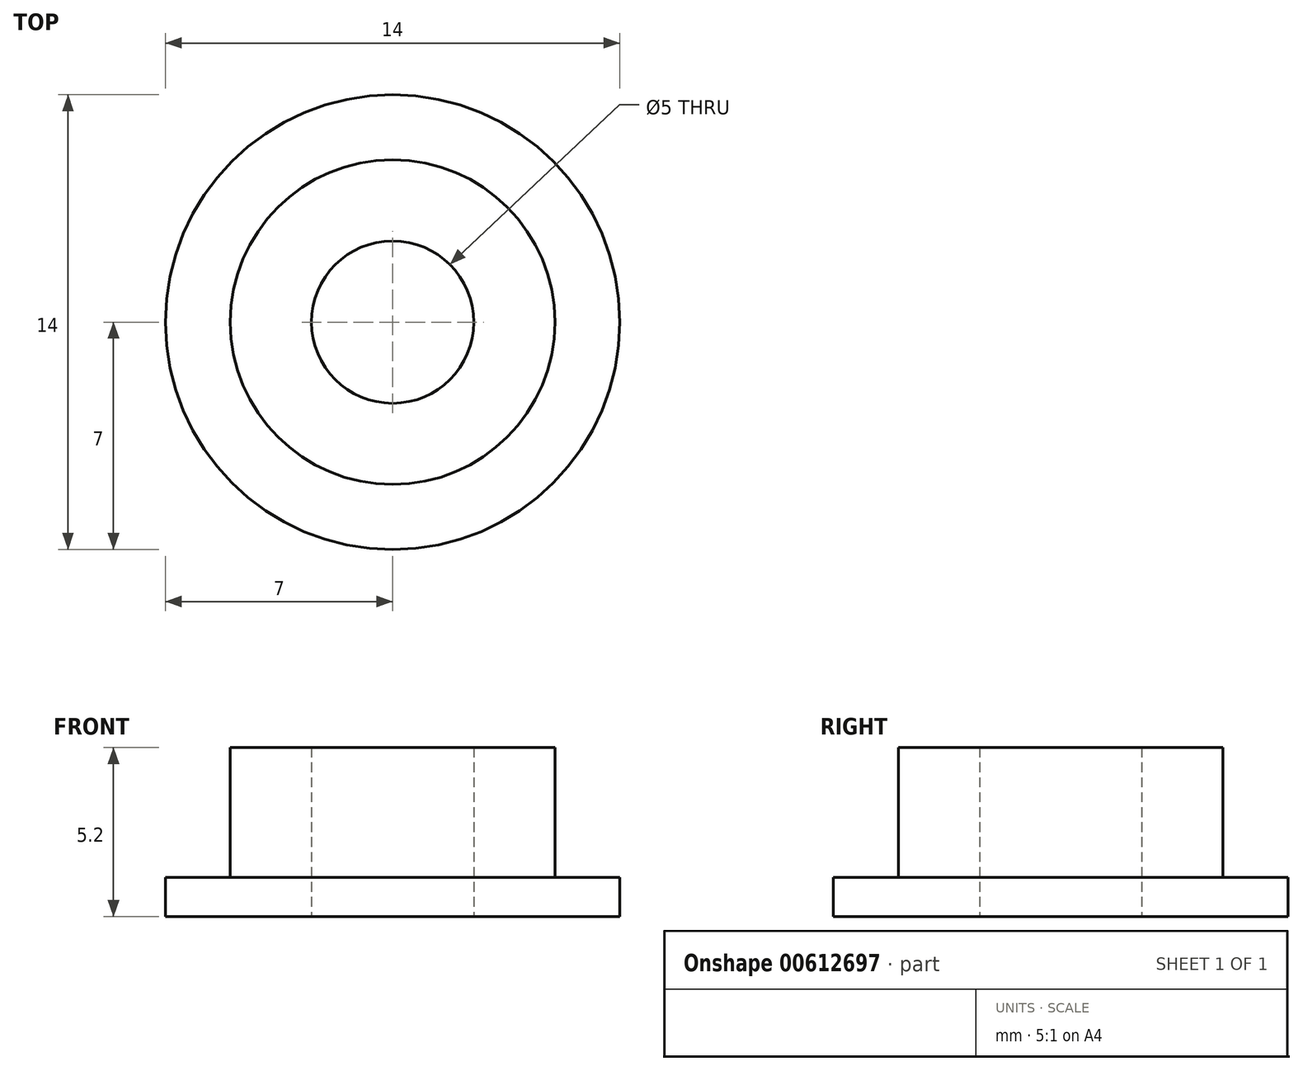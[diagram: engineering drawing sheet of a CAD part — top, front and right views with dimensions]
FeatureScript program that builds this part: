
annotation { "Feature Type Name" : "Feature", "Feature Type Description" : "" }
export const myFeature = defineFeature(function(context is Context, id is Id, definition is map)
    precondition{}
    {
        {
            var Q0;
            Q0=qCreatedBy(makeId("Front.planeOp"),FACE);
            var sketch = newSketch(context, id + "F0", { "sketchPlane" : qUnion([Q0])});
            skLineSegment(sketch, "E0", {"start": v(2.5, 0) * mm, "end": v(2.5, 5.2) * mm});
            skLineSegment(sketch, "E1", {"start": v(2.5, 5.2) * mm, "end": v(5, 5.2) * mm});
            skLineSegment(sketch, "E2", {"start": v(5, 5.2) * mm, "end": v(5, 1.2) * mm});
            skLineSegment(sketch, "E3", {"start": v(5, 1.2) * mm, "end": v(7, 1.2) * mm});
            skLineSegment(sketch, "E4", {"start": v(7, 1.2) * mm, "end": v(7, 0) * mm});
            skLineSegment(sketch, "E5", {"start": v(7, 0) * mm, "end": v(2.5, 0) * mm});
            skLineSegment(sketch, "E6", {"start": v(0, 0) * mm, "end": v(0, 5.2) * mm, "construction": true});
            skSolve(sketch);
        }
        {
            var Q0;
            Q0=makeQuery(id+"F0.imprint","IMPRINT",FACE,{"disambiguationData":[TD([[makeQuery(id+"F0.imprint","IMPRINT",EDGE,{"derivedFrom":sQuery(id+"F0.wireOp",EDGE,"E0")}),-1.0]])]});
            var Q1;
            Q1=sQuery(id+"F0.wireOp",EDGE,"E6");
            revolve(context, id + "F1", {"entities" : qUnion([Q0]), "axis" : qUnion([Q1]), "revolveType" : RevolveType.FULL});
        }
    });
